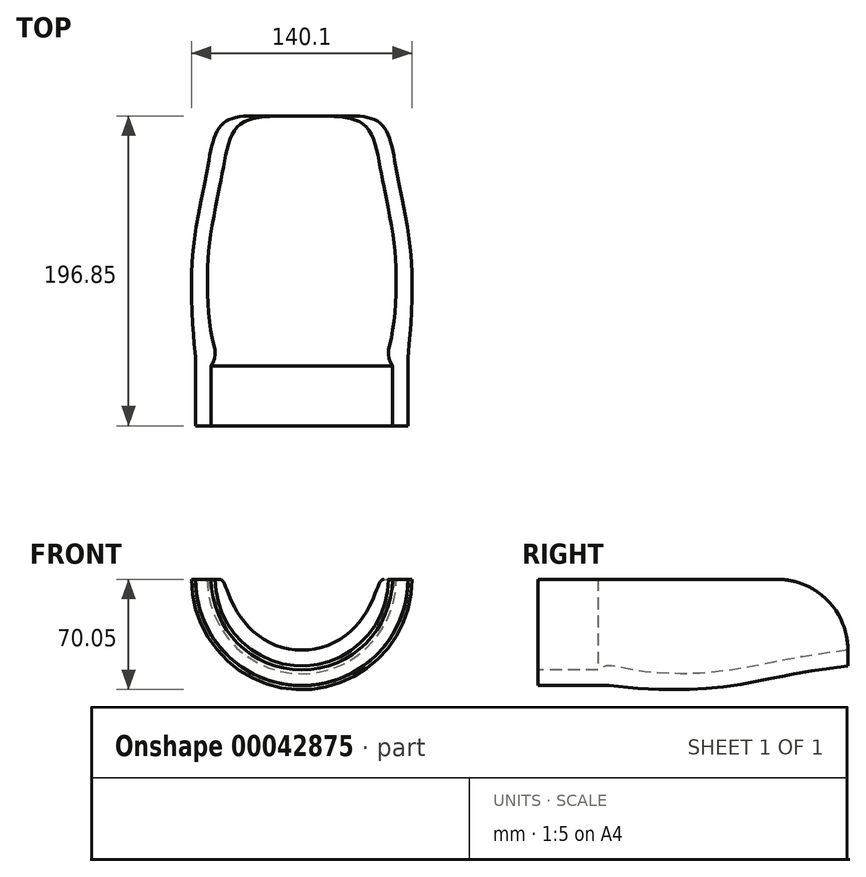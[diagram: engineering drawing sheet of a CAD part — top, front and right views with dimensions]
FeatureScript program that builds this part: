
annotation { "Feature Type Name" : "Feature", "Feature Type Description" : "" }
export const myFeature = defineFeature(function(context is Context, id is Id, definition is map)
    precondition{}
    {
        {
            var Q0;
            Q0=qCreatedBy(makeId("Top.planeOp"),FACE);
            var sketch = newSketch(context, id + "F0", { "sketchPlane" : qUnion([Q0])});
            skLineSegment(sketch, "E0", {"start": v(0, 76.2) * mm, "end": v(0, -76.2) * mm, "construction": true});
            skPoint(sketch, "E1", {"position": v(0, 0) * mm});
            skLineSegment(sketch, "E2", {"start": v(0, -76.2) * mm, "end": v(55, -76.2) * mm, "construction": true});
            skLineSegment(sketch, "E3", {"start": v(0, -61.2) * mm, "end": v(57.5, -61.2) * mm, "construction": true});
            skLineSegment(sketch, "E4", {"start": v(0, -27.2) * mm, "end": v(60, -27.2) * mm, "construction": true});
            skLineSegment(sketch, "E5", {"start": v(0, 2.8) * mm, "end": v(57.5, 2.8) * mm, "construction": true});
            skLineSegment(sketch, "E6", {"start": v(0, 42.8) * mm, "end": v(50, 42.8) * mm, "construction": true});
            skLineSegment(sketch, "E7", {"start": v(0, 76.2) * mm, "end": v(45, 76.2) * mm, "construction": true});
            skLineSegment(sketch, "E8.bottom", {"start": v(-157.02, 34.24) * mm, "end": v(-106.22, 34.24) * mm});
            skLineSegment(sketch, "E8.top", {"start": v(-157.02, -16.56) * mm, "end": v(-106.22, -16.56) * mm});
            skLineSegment(sketch, "E8.left", {"start": v(-157.02, 34.24) * mm, "end": v(-157.02, -16.56) * mm});
            skLineSegment(sketch, "E8.right", {"start": v(-106.22, 34.24) * mm, "end": v(-106.22, -16.56) * mm});
            skLineSegment(sketch, "E9", {"start": v(60, 76.2) * mm, "end": v(60, -76.2) * mm, "construction": true});
            skPoint(sketch, "E10", {"position": v(22.5, 76.2) * mm});
            skLineSegment(sketch, "E11", {"start": v(-60, 76.2) * mm, "end": v(-60, -76.2) * mm, "construction": true});
            skLineSegment(sketch, "E12", {"start": v(0, -101.6) * mm, "end": v(57.5, -101.6) * mm, "construction": true});
            skLineSegment(sketch, "E13", {"start": v(0, -120.65) * mm, "end": v(57.5, -120.65) * mm, "construction": true});
            skLineSegment(sketch, "E14", {"start": v(0, -82.55) * mm, "end": v(57.5, -82.55) * mm, "construction": true});
            skFitSpline(sketch, "E15", {"points": [v(45, 76.2) * mm, v(50, 42.8) * mm, v(57.5, 2.8) * mm, v(60, -27.2) * mm, v(57.5, -61.2) * mm, v(55, -76.2) * mm, v(57.5, -82.55) * mm], "startDerivative": vector(22.19, -166.26) * mm, "endDerivative": vector(39.07, -66.87) * mm});
            skLineSegment(sketch, "E16", {"start": v(57.5, -82.55) * mm, "end": v(57.5, -120.65) * mm});
            skLineSegment(sketch, "E17.filletArc", {"start": v(57.5, -82.55) * mm, "end": v(57.5, -82.55) * mm});
            skLineSegment(sketch, "E18", {"start": v(45, 76.2) * mm, "end": v(55, 76.2) * mm});
            skLineSegment(sketch, "E19", {"start": v(50, 42.8) * mm, "end": v(60, 42.8) * mm, "construction": true});
            skLineSegment(sketch, "E20", {"start": v(57.5, 2.8) * mm, "end": v(67.5, 2.8) * mm, "construction": true});
            skLineSegment(sketch, "E21", {"start": v(60, -27.2) * mm, "end": v(70, -27.2) * mm, "construction": true});
            skLineSegment(sketch, "E22", {"start": v(57.5, -61.2) * mm, "end": v(69, -61.2) * mm, "construction": true});
            skLineSegment(sketch, "E23", {"start": v(55, -76.2) * mm, "end": v(67.5, -76.2) * mm, "construction": true});
            skLineSegment(sketch, "E24", {"start": v(57.5, -82.55) * mm, "end": v(67.5, -82.55) * mm, "construction": true});
            skLineSegment(sketch, "E25", {"start": v(57.5, -101.6) * mm, "end": v(67.5, -101.6) * mm, "construction": true});
            skLineSegment(sketch, "E26", {"start": v(57.5, -120.65) * mm, "end": v(67.5, -120.65) * mm});
            skFitSpline(sketch, "E27", {"points": [v(55, 76.2) * mm, v(60, 42.8) * mm, v(67.5, 2.8) * mm, v(70, -27.2) * mm, v(69, -61.2) * mm, v(67.5, -76.2) * mm, v(67.5, -82.55) * mm, v(67.5, -101.6) * mm, v(67.5, -120.65) * mm], "startDerivative": vector(28.82, -213.97) * mm, "endDerivative": vector(-0.1, -161.58) * mm});
            skLineSegment(sketch, "E28", {"start": v(60, -76.2) * mm, "end": v(60, -137.07) * mm, "construction": true});
            skSolve(sketch);
        }
        {
            var Q0;
            Q0=makeQuery(id+"F0.imprint","IMPRINT",FACE,{"disambiguationData":[TD([[makeQuery(id+"F0.imprint","IMPRINT",EDGE,{"derivedFrom":sQuery(id+"F0.wireOp",EDGE,"E15")}),1.0]])]});
            var Q1;
            Q1=sQuery(id+"F0.wireOp",EDGE,"E0");
            revolve(context, id + "F1", {"entities" : qUnion([Q0]), "axis" : qUnion([Q1]), "revolveType" : RevolveType.ONE_DIRECTION, "oppositeDirection" : true, "angle" : 180 * degree});
        }
        {
            var Q0;
            Q0=makeQuery(id+"F1.opRevolve","CAP_EDGE",EDGE,{"disambiguationData":[OSD([sQuery(id+"F0.wireOp",EDGE,"E18")])],"isStart":true});
            var Q1;
            Q1=makeQuery(id+"F1.opRevolve","CAP_EDGE",EDGE,{"disambiguationData":[OSD([sQuery(id+"F0.wireOp",EDGE,"E18")])],"isStart":false});
            fillet(context, id + "F2", {"entities" : qUnion([Q0, Q1]), "radius" : 45 * mm, "tangentPropagation" : true, "allowEdgeOverflow" : false});
        }
        {
            var Q0;
            Q0=sQuery(id+"F0.wireOp",EDGE,"E9");
            var Q1;
            Q1=sQuery(id+"F0.wireOp",EDGE,"E11");
            cPlane(context, id + "F3", {"entities" : qUnion([Q0, Q1]), "cplaneType" : CPlaneType.LINE_ANGLE, "offset" : 150 * mm, "angle" : 90 * degree, "width" : 150 * mm, "height" : 150 * mm});
        }
        {
            var Q0;
            Q0=sQuery(id+"F0.wireOp",EDGE,"E11");
            cPlane(context, id + "F4", {"entities" : qUnion([Q0]), "cplaneType" : CPlaneType.LINE_ANGLE, "offset" : 150 * mm, "angle" : 90 * degree, "width" : 150 * mm, "height" : 150 * mm});
        }
    });
